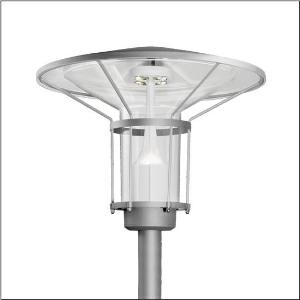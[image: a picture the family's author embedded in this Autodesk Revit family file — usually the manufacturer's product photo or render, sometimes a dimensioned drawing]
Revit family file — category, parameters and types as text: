
# Revit family: laterne_classic_iq___pl1_2s_5xa5245rf14h_f81d
name_source: partatom
category: Lighting Fixtures
units: mm (PartAtom-declared; Revit-internal decimal feet)

## family parameters
Cut with Voids When Loaded = No
Host = Face
Light Source = No
Part Type = Normal
Room Calculation Point = No
Round Connector Dimension = Use Diameter
Shared = No

## types (1)
- --- (1 x LED, 2670 lm, 18.5 W, 4000K)
    Apparent Load = 19 VA
    CIE Flux Codes = 21 60 93 97 100
    Color Rendering = 70
    Color Temperature = 4000K
    Default Elevation = 1800 mm
    Description = Lantern Classic iQ, mast luminaire, Module 540 iQ-SR, primary light control with 3 zone facetted reflector, of plastic, silver coated, highly specular, structured, primary optical cover: cover, of PMMA, transparent, light distribution: PL1.2s, light emission: direct distribution, primary light characteristic: symmetric, installation type: post-top, LED, High Power LED, rated luminous flux: 2.670lm, luminous efficacy: 144lm/W, light colour: 740, colour temperature: 4000K, control gear: ECG iQ, control: pre-setting: logarithmic dimming characteristic, Street-Remote, Auto-Match, Temp-Guard, Lumen-Switch, Night-Set, Smart-Wire, Light-Fading, Desk-Remote (wireless, voltage-free reading and setting of iQ features in the workshop via application-optimized NFC function/RFID function), optimised constant luminous flux control (CLO 2.0), with terminal, 6-pole, max. 2.5mm², mains connection: 230..240V, AC, 50/60Hz, start of lifetime: 19W, end of service life: 20W, reduction: 9W, luminaire housing, upper part, of glass-fibre reinforced polyester, coated, Siteco® metallic grey (DB 702S), diameter: 750mm, height: 596mm, spigot size: d x l = 76 x 70mm (post-top) | with reducer (optional accessory) 60 x 70mm, post-top mast mounting element, of diecast aluminium, coated, Siteco® metallic grey (DB 702S), Module 540 iQ-SR, traffic white (RAL 9016), equipment: standard, protection rating (complete): IP65, insulation class (complete): insulation class II (safety insulation), certification: CE, ENEC, VDE, packaging unit: 1 piece

Light Distribution: PL1.2s
    Height = 596 mm
    Lamp = 1 x LED
    Lamp Light Flux = 2670 lm
    Lamp Power = 18.5 W
    Lamp count = 1
    Length = 750 mm
    Luminous efficacy = 144 lm/W
    Manufacturer = Siteco
    ModVariant = No
    Model = 5XA5245RF14H
    Number of Poles = 1
    OnlyDefault = Yes
    Power Factor = 1
    Product Name = Laterne Classic iQ | PL1.2s
    Product group = mast luminaire | pylon top
    ProductGroupID = 6100
    Protection Class = Protection class II
    Protection Degree = IP 65
    RLX_Detail_Level = 1
    RLX_Emergency_Light_Flux = 0 lm
    RLX_Emergency_Type = 0
    RLX_Emergency_Type_DB = No
    RlxData = <blob elided: 62693 chars, md5=2d4d71ec>
    Socket = socket
    Standby Power = 0 W
    System Light Flux = 2670 lm
    System Power = 19 W
    Type Comments = factory setting: luminous flux: 100 % | dim-lin: 254 | 385 mA
    Type Image = l_1006052.jpg
    URL = http://relux.com
    VarID = @adj_115633
    Voltage = 0 V
    Weight = 0.00 kg
    Width = 0 mm  [stored 0 ft]

note: [stored X ft] marks values corroborated as IEEE doubles in the binary element streams (Revit-internal decimal feet)

## geometry (parser evidence)
native form markers: Blend x4, Sweep x8
no freeform markers — native parametric forms only
